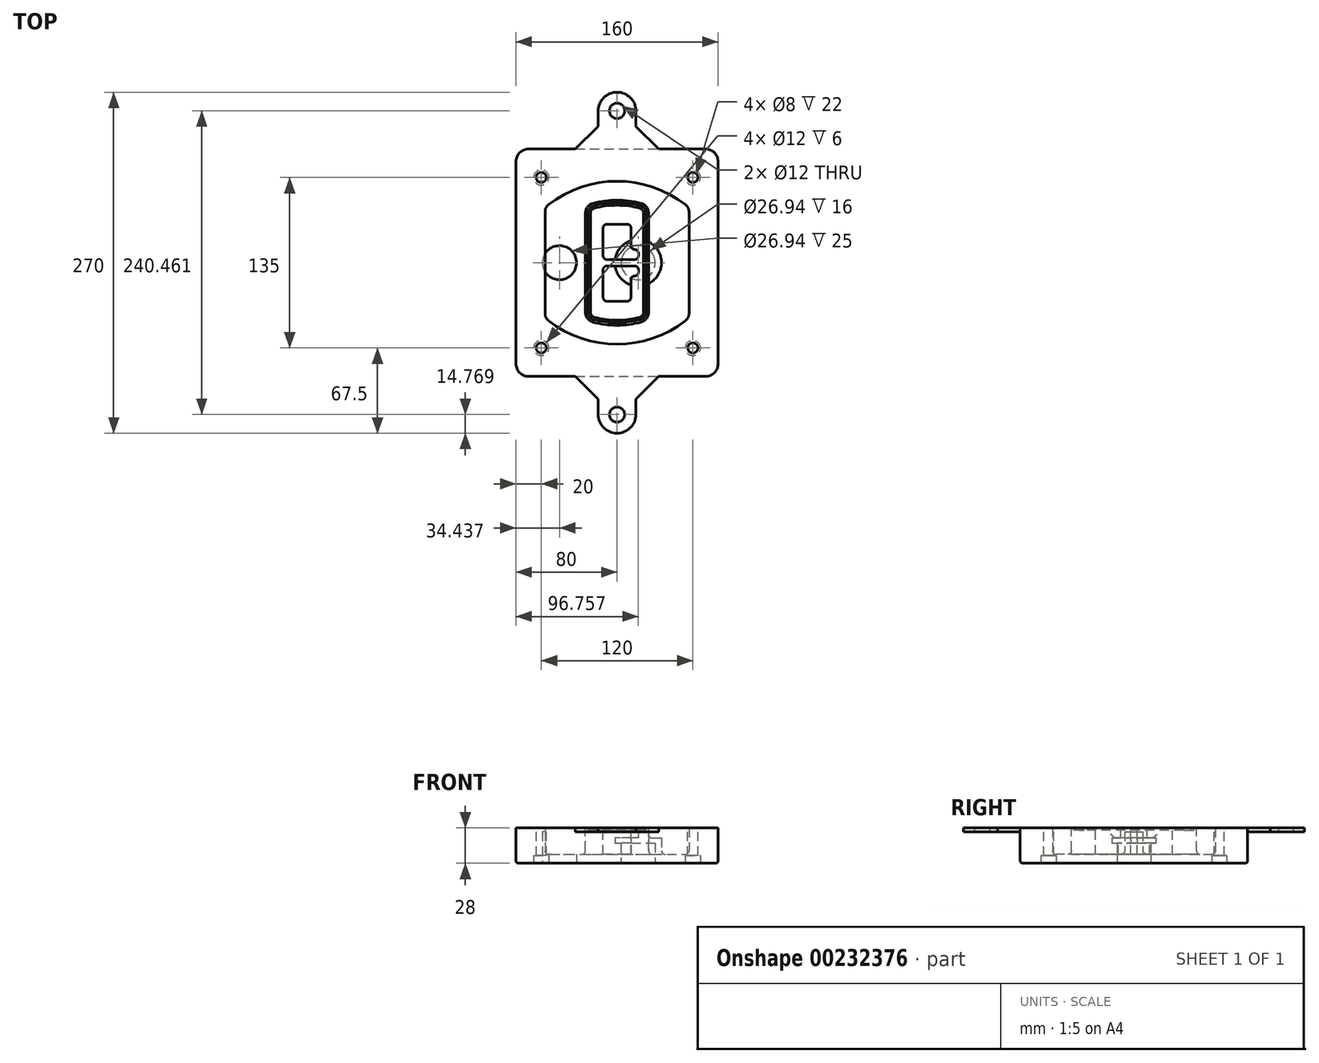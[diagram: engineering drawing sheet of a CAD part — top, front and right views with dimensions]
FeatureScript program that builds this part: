
annotation { "Feature Type Name" : "Feature", "Feature Type Description" : "" }
export const myFeature = defineFeature(function(context is Context, id is Id, definition is map)
    precondition{}
    {
        {
            var Q0;
            Q0=qCreatedBy(makeId("Top.planeOp"),FACE);
            var sketch = newSketch(context, id + "F0", { "sketchPlane" : qUnion([Q0])});
            skPoint(sketch, "E0.rect.middle", {"position": v(0, 0) * mm});
            skLineSegment(sketch, "E1.bottom", {"start": v(-70, -90) * mm, "end": v(70, -90) * mm});
            skLineSegment(sketch, "E1.top", {"start": v(-70, 90) * mm, "end": v(70, 90) * mm});
            skLineSegment(sketch, "E1.left", {"start": v(-80, -80) * mm, "end": v(-80, 80) * mm});
            skLineSegment(sketch, "E1.right", {"start": v(80, -80) * mm, "end": v(80, 80) * mm});
            skLineSegment(sketch, "E2", {"start": v(-80, 90) * mm, "end": v(80, -90) * mm, "construction": true});
            skLineSegment(sketch, "E3", {"start": v(80, 90) * mm, "end": v(-80, -90) * mm, "construction": true});
            skCircle(sketch, "E4", {"center": v(-60, 67.5) * mm, "radius": 4 * mm});
            skCircle(sketch, "E5", {"center": v(60, 67.5) * mm, "radius": 4 * mm});
            skCircle(sketch, "E6", {"center": v(60, -67.5) * mm, "radius": 4 * mm});
            skCircle(sketch, "E7", {"center": v(-60, -67.5) * mm, "radius": 4 * mm});
            skLineSegment(sketch, "E8", {"start": v(-60, 67.5) * mm, "end": v(60, 67.5) * mm, "construction": true});
            skLineSegment(sketch, "E9", {"start": v(60, 67.5) * mm, "end": v(60, -67.5) * mm, "construction": true});
            skLineSegment(sketch, "E10", {"start": v(60, -67.5) * mm, "end": v(-60, -67.5) * mm, "construction": true});
            skLineSegment(sketch, "E11", {"start": v(-60, -67.5) * mm, "end": v(-60, 67.5) * mm, "construction": true});
            skLineSegment(sketch, "E12", {"start": v(-60, 40.3) * mm, "end": v(-60, -40.3) * mm});
            skLineSegment(sketch, "E13", {"start": v(60, 40.3) * mm, "end": v(60, -40.3) * mm});
            skArc(sketch, "E14", {"start": v(56.15, 48.18) * mm, "mid": v(0, 67.5) * mm, "end": v(-56.15, 48.18) * mm});
            skArc(sketch, "E15", {"start": v(-56.15, -48.18) * mm, "mid": v(0, -67.5) * mm, "end": v(56.15, -48.18) * mm});
            skLineSegment(sketch, "E16", {"start": v(-60, 0) * mm, "end": v(60, 0) * mm, "construction": true});
            skPoint(sketch, "E17.visualSharp", {"position": v(-60, -45) * mm});
            skArc(sketch, "E17.filletArc", {"start": v(-60, -40.3) * mm, "mid": v(-58.99, -44.68) * mm, "end": v(-56.15, -48.18) * mm});
            skPoint(sketch, "E18.visualSharp", {"position": v(-60, 45) * mm});
            skArc(sketch, "E18.filletArc", {"start": v(-56.15, 48.18) * mm, "mid": v(-58.99, 44.68) * mm, "end": v(-60, 40.3) * mm});
            skPoint(sketch, "E19.visualSharp", {"position": v(60, 45) * mm});
            skArc(sketch, "E19.filletArc", {"start": v(60, 40.3) * mm, "mid": v(58.99, 44.68) * mm, "end": v(56.15, 48.18) * mm});
            skPoint(sketch, "E20.visualSharp", {"position": v(60, -45) * mm});
            skArc(sketch, "E20.filletArc", {"start": v(56.15, -48.18) * mm, "mid": v(58.99, -44.68) * mm, "end": v(60, -40.3) * mm});
            skPoint(sketch, "E21.visualSharp", {"position": v(-80, 90) * mm});
            skArc(sketch, "E21.filletArc", {"start": v(-70, 90) * mm, "mid": v(-77.07, 87.07) * mm, "end": v(-80, 80) * mm});
            skPoint(sketch, "E22.visualSharp", {"position": v(80, 90) * mm});
            skArc(sketch, "E22.filletArc", {"start": v(80, 80) * mm, "mid": v(77.07, 87.07) * mm, "end": v(70, 90) * mm});
            skPoint(sketch, "E23.visualSharp", {"position": v(80, -90) * mm});
            skArc(sketch, "E23.filletArc", {"start": v(70, -90) * mm, "mid": v(77.07, -87.07) * mm, "end": v(80, -80) * mm});
            skPoint(sketch, "E24.visualSharp", {"position": v(-80, -90) * mm});
            skArc(sketch, "E24.filletArc", {"start": v(-80, -80) * mm, "mid": v(-77.07, -87.07) * mm, "end": v(-70, -90) * mm});
            skArc(sketch, "E25.0", {"start": v(57, 40.3) * mm, "mid": v(56.3, 43.36) * mm, "end": v(54.3, 45.81) * mm});
            skLineSegment(sketch, "E25.1", {"start": v(57, 40.3) * mm, "end": v(57, -40.3) * mm});
            skArc(sketch, "E25.2", {"start": v(54.3, -45.81) * mm, "mid": v(56.3, -43.36) * mm, "end": v(57, -40.3) * mm});
            skArc(sketch, "E25.3", {"start": v(-54.3, -45.81) * mm, "mid": v(0, -64.5) * mm, "end": v(54.3, -45.81) * mm});
            skArc(sketch, "E25.4", {"start": v(-57, -40.3) * mm, "mid": v(-56.3, -43.36) * mm, "end": v(-54.3, -45.81) * mm});
            skArc(sketch, "E25.5", {"start": v(54.3, 45.81) * mm, "mid": v(0, 64.5) * mm, "end": v(-54.3, 45.81) * mm});
            skLineSegment(sketch, "E25.6", {"start": v(-57, 40.3) * mm, "end": v(-57, -40.3) * mm});
            skArc(sketch, "E25.7", {"start": v(-54.3, 45.81) * mm, "mid": v(-56.3, 43.36) * mm, "end": v(-57, 40.3) * mm});
            skArc(sketch, "E26.0", {"start": v(-58.62, 51.33) * mm, "mid": v(-62.58, 46.43) * mm, "end": v(-64, 40.3) * mm});
            skArc(sketch, "E26.1", {"start": v(58.62, 51.33) * mm, "mid": v(0, 71.5) * mm, "end": v(-58.62, 51.33) * mm});
            skArc(sketch, "E26.2", {"start": v(64, 40.3) * mm, "mid": v(62.58, 46.43) * mm, "end": v(58.62, 51.33) * mm});
            skLineSegment(sketch, "E26.3", {"start": v(64, 40.3) * mm, "end": v(64, -40.3) * mm});
            skArc(sketch, "E26.4", {"start": v(58.62, -51.33) * mm, "mid": v(62.58, -46.43) * mm, "end": v(64, -40.3) * mm});
            skLineSegment(sketch, "E26.5", {"start": v(-64, 40.3) * mm, "end": v(-64, -40.3) * mm});
            skArc(sketch, "E26.6", {"start": v(-58.62, -51.33) * mm, "mid": v(0, -71.5) * mm, "end": v(58.62, -51.33) * mm});
            skArc(sketch, "E26.7", {"start": v(-64, -40.3) * mm, "mid": v(-62.58, -46.43) * mm, "end": v(-58.62, -51.33) * mm});
            skSolve(sketch);
        }
        {
            var Q0;
            Q0=makeQuery(id+"F0.imprint","IMPRINT",FACE,{"disambiguationData":[TD([[makeQuery(id+"F0.imprint","IMPRINT",EDGE,{"derivedFrom":sQuery(id+"F0.wireOp",EDGE,"E1.bottom")}),1.0]])]});
            var Q1;
            Q1=makeQuery(id+"F0.imprint","IMPRINT",FACE,{"disambiguationData":[TD([[makeQuery(id+"F0.imprint","IMPRINT",EDGE,{"derivedFrom":sQuery(id+"F0.wireOp",EDGE,"E12")}),1.0]])]});
            var Q2;
            Q2=makeQuery(id+"F0.imprint","IMPRINT",FACE,{"disambiguationData":[TD([[makeQuery(id+"F0.imprint","IMPRINT",EDGE,{"derivedFrom":sQuery(id+"F0.wireOp",EDGE,"E25.0")}),1.0]])]});
            var Q3;
            Q3=makeQuery(id+"F0.imprint","IMPRINT",FACE,{"disambiguationData":[TD([[makeQuery(id+"F0.imprint","IMPRINT",EDGE,{"derivedFrom":sQuery(id+"F0.wireOp",EDGE,"E12")}),-1.0]])]});
            extrude(context, id + "F1", {"entities" : qUnion([Q0, Q1, Q2, Q3]), "oppositeDirection" : true, "depth" : 25 * mm});
        }
        {
            var Q0;
            Q0=makeQuery(id+"F0.imprint","IMPRINT",FACE,{"disambiguationData":[TD([[makeQuery(id+"F0.imprint","IMPRINT",EDGE,{"derivedFrom":sQuery(id+"F0.wireOp",EDGE,"E12")}),1.0]])]});
            extrude(context, id + "F2", {"entities" : qUnion([Q0]), "operationType" : NewBodyOperationType.ADD, "depth" : 3 * mm});
        }
        {
            var Q0;
            Q0=makeQuery(id+"F0.imprint","IMPRINT",FACE,{"disambiguationData":[TD([[makeQuery(id+"F0.imprint","IMPRINT",EDGE,{"derivedFrom":sQuery(id+"F0.wireOp",EDGE,"E25.0")}),1.0]])]});
            extrude(context, id + "F3", {"entities" : qUnion([Q0]), "operationType" : NewBodyOperationType.REMOVE, "oppositeDirection" : true, "depth" : 18 * mm});
        }
        {
            var Q0;
            Q0=makeQuery(id+"F2.opExtrude","CAP_FACE",FACE,{"disambiguationData":[OSD([sQuery(id+"F0.wireOp",EDGE,"E12"),sQuery(id+"F0.wireOp",EDGE,"E13"),sQuery(id+"F0.wireOp",EDGE,"E14"),sQuery(id+"F0.wireOp",EDGE,"E15"),sQuery(id+"F0.wireOp",EDGE,"E17.filletArc"),sQuery(id+"F0.wireOp",EDGE,"E18.filletArc"),sQuery(id+"F0.wireOp",EDGE,"E19.filletArc"),sQuery(id+"F0.wireOp",EDGE,"E20.filletArc"),sQuery(id+"F0.wireOp",EDGE,"E25.0"),sQuery(id+"F0.wireOp",EDGE,"E25.1"),sQuery(id+"F0.wireOp",EDGE,"E25.2"),sQuery(id+"F0.wireOp",EDGE,"E25.3"),sQuery(id+"F0.wireOp",EDGE,"E25.4"),sQuery(id+"F0.wireOp",EDGE,"E25.5"),sQuery(id+"F0.wireOp",EDGE,"E25.6"),sQuery(id+"F0.wireOp",EDGE,"E25.7")])],"isStart":false});
            var sketch = newSketch(context, id + "F4", { "sketchPlane" : qUnion([Q0])});
            skArc(sketch, "E27.0", {"start": v(-19.08, -46.97) * mm, "mid": v(0, -49.5) * mm, "end": v(19.08, -46.97) * mm});
            skArc(sketch, "E28.0", {"start": v(19.08, 46.97) * mm, "mid": v(0, 49.5) * mm, "end": v(-19.08, 46.97) * mm});
            skLineSegment(sketch, "E29", {"start": v(-25, 39.25) * mm, "end": v(-25, -39.25) * mm});
            skLineSegment(sketch, "E30", {"start": v(25, 39.25) * mm, "end": v(25, -39.25) * mm});
            skLineSegment(sketch, "E31", {"start": v(-25, 45.1) * mm, "end": v(25, 45.1) * mm, "construction": true});
            skLineSegment(sketch, "E32", {"start": v(-25, -45.1) * mm, "end": v(25, -45.1) * mm, "construction": true});
            skPoint(sketch, "E33.visualSharp", {"position": v(-25, 45.1) * mm});
            skArc(sketch, "E33.filletArc", {"start": v(-19.08, 46.97) * mm, "mid": v(-23.35, 44.11) * mm, "end": v(-25, 39.25) * mm});
            skPoint(sketch, "E34.visualSharp", {"position": v(25, 45.1) * mm});
            skArc(sketch, "E34.filletArc", {"start": v(25, 39.25) * mm, "mid": v(23.35, 44.11) * mm, "end": v(19.08, 46.97) * mm});
            skPoint(sketch, "E35.visualSharp", {"position": v(25, -45.1) * mm});
            skArc(sketch, "E35.filletArc", {"start": v(19.08, -46.97) * mm, "mid": v(23.35, -44.11) * mm, "end": v(25, -39.25) * mm});
            skPoint(sketch, "E36.visualSharp", {"position": v(-25, -45.1) * mm});
            skArc(sketch, "E36.filletArc", {"start": v(-25, -39.25) * mm, "mid": v(-23.35, -44.11) * mm, "end": v(-19.08, -46.97) * mm});
            skArc(sketch, "E37.0", {"start": v(54.3, 45.81) * mm, "mid": v(0, 64.5) * mm, "end": v(-54.3, 45.81) * mm});
            skArc(sketch, "E37.1", {"start": v(-54.3, 45.81) * mm, "mid": v(-56.3, 43.36) * mm, "end": v(-57, 40.3) * mm});
            skLineSegment(sketch, "E37.2", {"start": v(-57, 40.3) * mm, "end": v(-57, -40.3) * mm});
            skArc(sketch, "E37.3", {"start": v(-57, -40.3) * mm, "mid": v(-56.3, -43.36) * mm, "end": v(-54.3, -45.81) * mm});
            skArc(sketch, "E37.4", {"start": v(-54.3, -45.81) * mm, "mid": v(0, -64.5) * mm, "end": v(54.3, -45.81) * mm});
            skArc(sketch, "E37.5", {"start": v(54.3, -45.81) * mm, "mid": v(56.3, -43.36) * mm, "end": v(57, -40.3) * mm});
            skLineSegment(sketch, "E37.6", {"start": v(57, 40.3) * mm, "end": v(57, -40.3) * mm});
            skArc(sketch, "E37.7", {"start": v(57, 40.3) * mm, "mid": v(56.3, 43.36) * mm, "end": v(54.3, 45.81) * mm});
            skLineSegment(sketch, "E38.0", {"start": v(23, 39.25) * mm, "end": v(23, -39.25) * mm});
            skArc(sketch, "E38.1", {"start": v(18.56, -45.04) * mm, "mid": v(21.76, -42.9) * mm, "end": v(23, -39.25) * mm});
            skArc(sketch, "E38.2", {"start": v(-18.56, -45.04) * mm, "mid": v(0, -47.5) * mm, "end": v(18.56, -45.04) * mm});
            skArc(sketch, "E38.3", {"start": v(-23, -39.25) * mm, "mid": v(-21.76, -42.9) * mm, "end": v(-18.56, -45.04) * mm});
            skLineSegment(sketch, "E38.4", {"start": v(-23, 39.25) * mm, "end": v(-23, -39.25) * mm});
            skArc(sketch, "E38.5", {"start": v(23, 39.25) * mm, "mid": v(21.76, 42.9) * mm, "end": v(18.56, 45.04) * mm});
            skArc(sketch, "E38.6", {"start": v(-18.56, 45.04) * mm, "mid": v(-21.76, 42.9) * mm, "end": v(-23, 39.25) * mm});
            skArc(sketch, "E38.7", {"start": v(18.56, 45.04) * mm, "mid": v(0, 47.5) * mm, "end": v(-18.56, 45.04) * mm});
            skArc(sketch, "E39.0", {"start": v(21, 39.25) * mm, "mid": v(20.18, 41.68) * mm, "end": v(18.04, 43.1) * mm});
            skLineSegment(sketch, "E39.1", {"start": v(21, 39.25) * mm, "end": v(21, -39.25) * mm});
            skArc(sketch, "E39.2", {"start": v(18.04, -43.1) * mm, "mid": v(20.18, -41.68) * mm, "end": v(21, -39.25) * mm});
            skArc(sketch, "E39.3", {"start": v(-18.04, -43.1) * mm, "mid": v(0, -45.5) * mm, "end": v(18.04, -43.1) * mm});
            skArc(sketch, "E39.4", {"start": v(-21, -39.25) * mm, "mid": v(-20.18, -41.68) * mm, "end": v(-18.04, -43.1) * mm});
            skArc(sketch, "E39.5", {"start": v(18.04, 43.1) * mm, "mid": v(0, 45.5) * mm, "end": v(-18.04, 43.1) * mm});
            skLineSegment(sketch, "E39.6", {"start": v(-21, 39.25) * mm, "end": v(-21, -39.25) * mm});
            skArc(sketch, "E39.7", {"start": v(-18.04, 43.1) * mm, "mid": v(-20.18, 41.68) * mm, "end": v(-21, 39.25) * mm});
            skLineSegment(sketch, "E40", {"start": v(-25, 0) * mm, "end": v(25, 0) * mm, "construction": true});
            skLineSegment(sketch, "E41", {"start": v(-11, 5.5) * mm, "end": v(-11, 27.5) * mm});
            skLineSegment(sketch, "E42", {"start": v(-8, 30.5) * mm, "end": v(8, 30.5) * mm});
            skLineSegment(sketch, "E43", {"start": v(11, 27.5) * mm, "end": v(11, 13.5) * mm});
            skLineSegment(sketch, "E44", {"start": v(14, 10.5) * mm, "end": v(14, 10.5) * mm});
            skLineSegment(sketch, "E45", {"start": v(17, 7.5) * mm, "end": v(17, 5.5) * mm});
            skLineSegment(sketch, "E46", {"start": v(14, 2.5) * mm, "end": v(-8, 2.5) * mm});
            skPoint(sketch, "E47.visualSharp", {"position": v(-11, 30.5) * mm});
            skArc(sketch, "E47.filletArc", {"start": v(-8, 30.5) * mm, "mid": v(-10.12, 29.62) * mm, "end": v(-11, 27.5) * mm});
            skPoint(sketch, "E48.visualSharp", {"position": v(11, 30.5) * mm});
            skArc(sketch, "E48.filletArc", {"start": v(11, 27.5) * mm, "mid": v(10.12, 29.62) * mm, "end": v(8, 30.5) * mm});
            skPoint(sketch, "E49.visualSharp", {"position": v(11, 10.5) * mm});
            skArc(sketch, "E49.filletArc", {"start": v(11, 13.5) * mm, "mid": v(11.88, 11.38) * mm, "end": v(14, 10.5) * mm});
            skPoint(sketch, "E50.visualSharp", {"position": v(17, 10.5) * mm});
            skArc(sketch, "E50.filletArc", {"start": v(17, 7.5) * mm, "mid": v(16.12, 9.62) * mm, "end": v(14, 10.5) * mm});
            skPoint(sketch, "E51.visualSharp", {"position": v(17, 2.5) * mm});
            skArc(sketch, "E51.filletArc", {"start": v(14, 2.5) * mm, "mid": v(16.12, 3.38) * mm, "end": v(17, 5.5) * mm});
            skPoint(sketch, "E52.visualSharp", {"position": v(-11, 2.5) * mm});
            skArc(sketch, "E52.filletArc", {"start": v(-11, 5.5) * mm, "mid": v(-10.12, 3.38) * mm, "end": v(-8, 2.5) * mm});
            skLineSegment(sketch, "E53.0.MirrorCS", {"start": v(14, -2.5) * mm, "end": v(-8, -2.5) * mm});
            skArc(sketch, "E54.0.MirrorCS", {"start": v(-11, -5.5) * mm, "mid": v(-10.12, -3.38) * mm, "end": v(-8, -2.5) * mm});
            skLineSegment(sketch, "E55.0.MirrorCS", {"start": v(-11, -5.5) * mm, "end": v(-11, -27.5) * mm});
            skArc(sketch, "E56.0.MirrorCS", {"start": v(-8, -30.5) * mm, "mid": v(-10.12, -29.62) * mm, "end": v(-11, -27.5) * mm});
            skLineSegment(sketch, "E57.0.MirrorCS", {"start": v(-8, -30.5) * mm, "end": v(8, -30.5) * mm});
            skArc(sketch, "E58.0.MirrorCS", {"start": v(11, -27.5) * mm, "mid": v(10.12, -29.62) * mm, "end": v(8, -30.5) * mm});
            skLineSegment(sketch, "E59.0.MirrorCS", {"start": v(11, -27.5) * mm, "end": v(11, -13.5) * mm});
            skArc(sketch, "E60.0.MirrorCS", {"start": v(11, -13.5) * mm, "mid": v(11.88, -11.38) * mm, "end": v(14, -10.5) * mm});
            skArc(sketch, "E61.0.MirrorCS", {"start": v(17, -7.5) * mm, "mid": v(16.12, -9.62) * mm, "end": v(14, -10.5) * mm});
            skLineSegment(sketch, "E62.0.MirrorCS", {"start": v(17, -7.5) * mm, "end": v(17, -5.5) * mm});
            skArc(sketch, "E63.0.MirrorCS", {"start": v(14, -2.5) * mm, "mid": v(16.12, -3.38) * mm, "end": v(17, -5.5) * mm});
            skSolve(sketch);
        }
        {
            var Q0;
            Q0=makeQuery(id+"F4.imprint","IMPRINT",FACE,{"disambiguationData":[TD([[makeQuery(id+"F4.imprint","IMPRINT",EDGE,{"derivedFrom":sQuery(id+"F4.wireOp",EDGE,"E27.0")}),1.0]])]});
            var Q1;
            Q1=makeQuery(id+"F4.imprint","IMPRINT",FACE,{"disambiguationData":[TD([[makeQuery(id+"F4.imprint","IMPRINT",EDGE,{"derivedFrom":sQuery(id+"F4.wireOp",EDGE,"E38.0")}),-1.0]])]});
            var Q2;
            Q2=makeQuery(id+"F4.imprint","IMPRINT",FACE,{"disambiguationData":[TD([[makeQuery(id+"F4.imprint","IMPRINT",EDGE,{"derivedFrom":sQuery(id+"F4.wireOp",EDGE,"E39.0")}),1.0]])]});
            extrude(context, id + "F5", {"entities" : qUnion([Q0, Q1, Q2]), "operationType" : NewBodyOperationType.ADD, "endBound" : BoundingType.UP_TO_NEXT, "oppositeDirection" : true, "depth" : 25 * mm});
        }
        {
            var Q0;
            Q0=makeQuery(id+"F4.imprint","IMPRINT",FACE,{"disambiguationData":[TD([[makeQuery(id+"F4.imprint","IMPRINT",EDGE,{"derivedFrom":sQuery(id+"F4.wireOp",EDGE,"E38.0")}),-1.0]])]});
            extrude(context, id + "F6", {"entities" : qUnion([Q0]), "operationType" : NewBodyOperationType.REMOVE, "oppositeDirection" : true, "depth" : 2 * mm});
        }
        {
            var Q0;
            Q0=makeQuery(id+"F1.opExtrude","CAP_FACE",FACE,{"disambiguationData":[OSD([sQuery(id+"F0.wireOp",EDGE,"E1.bottom"),sQuery(id+"F0.wireOp",EDGE,"E1.top"),sQuery(id+"F0.wireOp",EDGE,"E1.left"),sQuery(id+"F0.wireOp",EDGE,"E1.right"),sQuery(id+"F0.wireOp",EDGE,"E4"),sQuery(id+"F0.wireOp",EDGE,"E5"),sQuery(id+"F0.wireOp",EDGE,"E6"),sQuery(id+"F0.wireOp",EDGE,"E7"),sQuery(id+"F0.wireOp",EDGE,"E21.filletArc"),sQuery(id+"F0.wireOp",EDGE,"E22.filletArc"),sQuery(id+"F0.wireOp",EDGE,"E23.filletArc"),sQuery(id+"F0.wireOp",EDGE,"E24.filletArc")])],"isStart":false});
            var sketch = newSketch(context, id + "F7", { "sketchPlane" : qUnion([Q0])});
            skCircle(sketch, "E64", {"center": v(16.76, 0) * mm, "radius": 13.47 * mm});
            skCircle(sketch, "E65", {"center": v(-45.56, 0) * mm, "radius": 13.47 * mm});
            skLineSegment(sketch, "E66", {"start": v(80, 0) * mm, "end": v(-80, 0) * mm});
            skCircle(sketch, "E67", {"center": v(16.76, 0) * mm, "radius": 18.47 * mm});
            skCircle(sketch, "E68", {"center": v(60, -67.5) * mm, "radius": 6 * mm});
            skCircle(sketch, "E69", {"center": v(-60, -67.5) * mm, "radius": 6 * mm});
            skCircle(sketch, "E70", {"center": v(-60, 67.5) * mm, "radius": 6 * mm});
            skCircle(sketch, "E71", {"center": v(60, 67.5) * mm, "radius": 6 * mm});
            skSolve(sketch);
        }
        {
            var Q0;
            {var subQ1=sQuery(id+"F7.wireOp",EDGE,"E66");var subQ4=sQuery(id+"F7.wireOp",EDGE,"E64");var subQ6=makeQuery(id+"F7.imprint","INTERSECT",VERTEX,{"disambiguationData":[OD(0.0)],"derivedFrom":[subQ4,subQ1]});Q0=makeQuery(id+"F7.imprint","IMPRINT",FACE,{"disambiguationData":[TD([[makeQuery(id+"F7.imprint","IMPRINT",EDGE,{"disambiguationData":[TD([[subQ6,-1.0]])],"derivedFrom":subQ4}),-1.0]])]});}
            var Q1;
            {var subQ0=sQuery(id+"F7.wireOp",EDGE,"E66");var subQ1=sQuery(id+"F7.wireOp",EDGE,"E64");var subQ3=makeQuery(id+"F7.imprint","INTERSECT",VERTEX,{"disambiguationData":[OD(0.0)],"derivedFrom":[subQ1,subQ0]});Q1=makeQuery(id+"F7.imprint","IMPRINT",FACE,{"disambiguationData":[TD([[makeQuery(id+"F7.imprint","IMPRINT",EDGE,{"disambiguationData":[TD([[subQ3,-1.0]])],"derivedFrom":subQ1}),1.0]])]});}
            var Q2;
            {var subQ0=sQuery(id+"F7.wireOp",EDGE,"E66");var subQ1=sQuery(id+"F7.wireOp",EDGE,"E64");var subQ3=makeQuery(id+"F7.imprint","INTERSECT",VERTEX,{"disambiguationData":[OD(0.0)],"derivedFrom":[subQ1,subQ0]});Q2=makeQuery(id+"F7.imprint","IMPRINT",FACE,{"disambiguationData":[TD([[makeQuery(id+"F7.imprint","IMPRINT",EDGE,{"disambiguationData":[TD([[subQ3,1.0]])],"derivedFrom":subQ1}),1.0]])]});}
            var Q3;
            {var subQ1=sQuery(id+"F7.wireOp",EDGE,"E66");var subQ4=sQuery(id+"F7.wireOp",EDGE,"E64");var subQ6=makeQuery(id+"F7.imprint","INTERSECT",VERTEX,{"disambiguationData":[OD(0.0)],"derivedFrom":[subQ4,subQ1]});Q3=makeQuery(id+"F7.imprint","IMPRINT",FACE,{"disambiguationData":[TD([[makeQuery(id+"F7.imprint","IMPRINT",EDGE,{"disambiguationData":[TD([[subQ6,1.0]])],"derivedFrom":subQ4}),-1.0]])]});}
            extrude(context, id + "F8", {"entities" : qUnion([Q0, Q1, Q2, Q3]), "operationType" : NewBodyOperationType.ADD, "oppositeDirection" : true, "depth" : 20 * mm});
        }
        {
            var Q0;
            {var subQ0=sQuery(id+"F7.wireOp",EDGE,"E66");var subQ1=sQuery(id+"F7.wireOp",EDGE,"E64");var subQ3=makeQuery(id+"F7.imprint","INTERSECT",VERTEX,{"disambiguationData":[OD(0.0)],"derivedFrom":[subQ1,subQ0]});Q0=makeQuery(id+"F7.imprint","IMPRINT",FACE,{"disambiguationData":[TD([[makeQuery(id+"F7.imprint","IMPRINT",EDGE,{"disambiguationData":[TD([[subQ3,-1.0]])],"derivedFrom":subQ1}),1.0]])]});}
            var Q1;
            {var subQ0=sQuery(id+"F7.wireOp",EDGE,"E66");var subQ1=sQuery(id+"F7.wireOp",EDGE,"E64");var subQ3=makeQuery(id+"F7.imprint","INTERSECT",VERTEX,{"disambiguationData":[OD(0.0)],"derivedFrom":[subQ1,subQ0]});Q1=makeQuery(id+"F7.imprint","IMPRINT",FACE,{"disambiguationData":[TD([[makeQuery(id+"F7.imprint","IMPRINT",EDGE,{"disambiguationData":[TD([[subQ3,1.0]])],"derivedFrom":subQ1}),1.0]])]});}
            extrude(context, id + "F9", {"entities" : qUnion([Q0, Q1]), "operationType" : NewBodyOperationType.REMOVE, "oppositeDirection" : true, "depth" : 16 * mm});
        }
        {
            var Q0;
            {var subQ0=sQuery(id+"F7.wireOp",EDGE,"E66");var subQ1=sQuery(id+"F7.wireOp",EDGE,"E65");var subQ3=makeQuery(id+"F7.imprint","INTERSECT",VERTEX,{"disambiguationData":[OD(0.0)],"derivedFrom":[subQ1,subQ0]});Q0=makeQuery(id+"F7.imprint","IMPRINT",FACE,{"disambiguationData":[TD([[makeQuery(id+"F7.imprint","IMPRINT",EDGE,{"disambiguationData":[TD([[subQ3,-1.0]])],"derivedFrom":subQ1}),1.0]])]});}
            var Q1;
            {var subQ0=sQuery(id+"F7.wireOp",EDGE,"E66");var subQ1=sQuery(id+"F7.wireOp",EDGE,"E65");var subQ3=makeQuery(id+"F7.imprint","INTERSECT",VERTEX,{"disambiguationData":[OD(0.0)],"derivedFrom":[subQ1,subQ0]});Q1=makeQuery(id+"F7.imprint","IMPRINT",FACE,{"disambiguationData":[TD([[makeQuery(id+"F7.imprint","IMPRINT",EDGE,{"disambiguationData":[TD([[subQ3,1.0]])],"derivedFrom":subQ1}),1.0]])]});}
            extrude(context, id + "F10", {"entities" : qUnion([Q0, Q1]), "operationType" : NewBodyOperationType.REMOVE, "oppositeDirection" : true, "depth" : 25 * mm});
        }
        {
            var Q0;
            Q0=makeQuery(id+"F7.imprint","IMPRINT",FACE,{"disambiguationData":[TD([[makeQuery(id+"F7.imprint","IMPRINT",EDGE,{"derivedFrom":sQuery(id+"F7.wireOp",EDGE,"E68")}),1.0]])]});
            var Q1;
            Q1=makeQuery(id+"F7.imprint","IMPRINT",FACE,{"disambiguationData":[TD([[makeQuery(id+"F7.imprint","IMPRINT",EDGE,{"derivedFrom":makeQuery(id+"F1.opExtrude","CAP_EDGE",EDGE,{"disambiguationData":[OSD([sQuery(id+"F0.wireOp",EDGE,"E5")])],"isStart":false})}),-1.0]])]});
            var Q2;
            Q2=makeQuery(id+"F7.imprint","IMPRINT",FACE,{"disambiguationData":[TD([[makeQuery(id+"F7.imprint","IMPRINT",EDGE,{"derivedFrom":sQuery(id+"F7.wireOp",EDGE,"E69")}),1.0]])]});
            var Q3;
            Q3=makeQuery(id+"F7.imprint","IMPRINT",FACE,{"disambiguationData":[TD([[makeQuery(id+"F7.imprint","IMPRINT",EDGE,{"derivedFrom":makeQuery(id+"F1.opExtrude","CAP_EDGE",EDGE,{"disambiguationData":[OSD([sQuery(id+"F0.wireOp",EDGE,"E4")])],"isStart":false})}),-1.0]])]});
            var Q4;
            Q4=makeQuery(id+"F7.imprint","IMPRINT",FACE,{"disambiguationData":[TD([[makeQuery(id+"F7.imprint","IMPRINT",EDGE,{"derivedFrom":sQuery(id+"F7.wireOp",EDGE,"E70")}),1.0]])]});
            var Q5;
            Q5=makeQuery(id+"F7.imprint","IMPRINT",FACE,{"disambiguationData":[TD([[makeQuery(id+"F7.imprint","IMPRINT",EDGE,{"derivedFrom":makeQuery(id+"F1.opExtrude","CAP_EDGE",EDGE,{"disambiguationData":[OSD([sQuery(id+"F0.wireOp",EDGE,"E7")])],"isStart":false})}),-1.0]])]});
            var Q6;
            Q6=makeQuery(id+"F7.imprint","IMPRINT",FACE,{"disambiguationData":[TD([[makeQuery(id+"F7.imprint","IMPRINT",EDGE,{"derivedFrom":sQuery(id+"F7.wireOp",EDGE,"E71")}),1.0]])]});
            var Q7;
            Q7=makeQuery(id+"F7.imprint","IMPRINT",FACE,{"disambiguationData":[TD([[makeQuery(id+"F7.imprint","IMPRINT",EDGE,{"derivedFrom":makeQuery(id+"F1.opExtrude","CAP_EDGE",EDGE,{"disambiguationData":[OSD([sQuery(id+"F0.wireOp",EDGE,"E6")])],"isStart":false})}),-1.0]])]});
            extrude(context, id + "F11", {"entities" : qUnion([Q0, Q1, Q2, Q3, Q4, Q5, Q6, Q7]), "operationType" : NewBodyOperationType.REMOVE, "oppositeDirection" : true, "depth" : 6 * mm});
        }
        {
            var Q0;
            Q0=makeQuery(id+"F9.boolean.opBoolean","COPY",FACE,{"derivedFrom":makeQuery(id+"F9.opExtrude","CAP_FACE",FACE,{"disambiguationData":[OSD([sQuery(id+"F7.wireOp",EDGE,"E64")])],"isStart":false})});
            var sketch = newSketch(context, id + "F12", { "sketchPlane" : qUnion([Q0])});
            skArc(sketch, "E72.0", {"start": v(11, 17.55) * mm, "mid": v(2.57, 11.82) * mm, "end": v(-1.54, 2.5) * mm});
            skArc(sketch, "E72.1", {"start": v(-1.54, -2.5) * mm, "mid": v(2.57, -11.82) * mm, "end": v(11, -17.55) * mm});
            skLineSegment(sketch, "E73", {"start": v(-1.54, -2.5) * mm, "end": v(14, -2.5) * mm});
            skLineSegment(sketch, "E74.0", {"start": v(14, 2.5) * mm, "end": v(-1.54, 2.5) * mm});
            skArc(sketch, "E74.1", {"start": v(14, 2.5) * mm, "mid": v(16.12, 3.38) * mm, "end": v(17, 5.5) * mm});
            skLineSegment(sketch, "E74.2", {"start": v(17, 7.5) * mm, "end": v(17, 5.5) * mm});
            skArc(sketch, "E74.3", {"start": v(17, 7.5) * mm, "mid": v(16.12, 9.62) * mm, "end": v(14, 10.5) * mm});
            skArc(sketch, "E74.4", {"start": v(11, 13.5) * mm, "mid": v(11.88, 11.38) * mm, "end": v(14, 10.5) * mm});
            skLineSegment(sketch, "E74.5", {"start": v(11, 17.55) * mm, "end": v(11, 13.5) * mm});
            skLineSegment(sketch, "E74.7", {"start": v(14, -2.5) * mm, "end": v(-1.54, -2.5) * mm});
            skArc(sketch, "E74.8", {"start": v(14, -2.5) * mm, "mid": v(16.12, -3.38) * mm, "end": v(17, -5.5) * mm});
            skLineSegment(sketch, "E74.9", {"start": v(17, -7.5) * mm, "end": v(17, -5.5) * mm});
            skArc(sketch, "E74.10", {"start": v(17, -7.5) * mm, "mid": v(16.12, -9.62) * mm, "end": v(14, -10.5) * mm});
            skArc(sketch, "E74.11", {"start": v(11, -13.5) * mm, "mid": v(11.88, -11.38) * mm, "end": v(14, -10.5) * mm});
            skLineSegment(sketch, "E74.12", {"start": v(11, -17.55) * mm, "end": v(11, -13.5) * mm});
            skPoint(sketch, "E75.orphan", {"position": v(11, -27.5) * mm});
            skPoint(sketch, "E76.orphan", {"position": v(-8, -2.5) * mm});
            skPoint(sketch, "E77.orphan", {"position": v(-8, 2.5) * mm});
            skPoint(sketch, "E78.orphan", {"position": v(11, 27.5) * mm});
            skSolve(sketch);
        }
        {
            var Q0;
            {var subQ7=sQuery(id+"F12.wireOp",EDGE,"E72.0");var subQ14=sQuery(id+"F12.wireOp",EDGE,"E72.1");var subQ16=sQuery(id+"F12.wireOp",EDGE,"E74.1");var subQ18=sQuery(id+"F12.wireOp",EDGE,"E74.8");Q0=qUnion([makeQuery(id+"F12.imprint","IMPRINT",FACE,{"disambiguationData":[TD([[makeQuery(id+"F12.imprint","IMPRINT",EDGE,{"derivedFrom":subQ7}),1.0]])]}),makeQuery(id+"F12.imprint","IMPRINT",FACE,{"disambiguationData":[TD([[makeQuery(id+"F12.imprint","IMPRINT",EDGE,{"derivedFrom":subQ14}),1.0]])]}),makeQuery(id+"F12.imprint","IMPRINT",FACE,{"disambiguationData":[TD([[makeQuery(id+"F12.imprint","IMPRINT",EDGE,{"derivedFrom":subQ16}),1.0]])]}),makeQuery(id+"F12.imprint","IMPRINT",FACE,{"disambiguationData":[TD([[makeQuery(id+"F12.imprint","IMPRINT",EDGE,{"derivedFrom":subQ18}),-1.0]])]})]);}
            var Q1;
            Q1=makeQuery(id+"F5.boolean.opBoolean","SPLIT",FACE,{"disambiguationData":[TD([makeQuery(id+"F5.opExtrude","SWEPT_FACE",FACE,{"disambiguationData":[OSD([sQuery(id+"F4.wireOp",EDGE,"E41")])]})])],"derivedFrom":makeQuery(id+"F3.boolean.opBoolean","COPY",FACE,{"derivedFrom":makeQuery(id+"F3.opExtrude","CAP_FACE",FACE,{"disambiguationData":[OSD([sQuery(id+"F0.wireOp",EDGE,"E25.0"),sQuery(id+"F0.wireOp",EDGE,"E25.1"),sQuery(id+"F0.wireOp",EDGE,"E25.2"),sQuery(id+"F0.wireOp",EDGE,"E25.3"),sQuery(id+"F0.wireOp",EDGE,"E25.4"),sQuery(id+"F0.wireOp",EDGE,"E25.5"),sQuery(id+"F0.wireOp",EDGE,"E25.6"),sQuery(id+"F0.wireOp",EDGE,"E25.7")])],"isStart":false})})});
            extrude(context, id + "F13", {"entities" : qUnion([Q0]), "operationType" : NewBodyOperationType.REMOVE, "endBound" : BoundingType.UP_TO_SURFACE, "endBoundEntityFace" : qUnion([Q1]), "depth" : 25 * mm});
        }
        {
            var Q0;
            Q0=makeQuery(id+"F3.boolean.opBoolean","COPY",EDGE,{"derivedFrom":makeQuery(id+"F3.opExtrude","CAP_EDGE",EDGE,{"disambiguationData":[OSD([sQuery(id+"F0.wireOp",EDGE,"E25.6")])],"isStart":false})});
            var Q1;
            Q1=makeQuery(id+"F8.boolean.opBoolean","INTERSECT",EDGE,{"derivedFrom":[makeQuery(id+"F5.opExtrude","SWEPT_FACE",FACE,{"disambiguationData":[OSD([sQuery(id+"F4.wireOp",EDGE,"E30")])]}),makeQuery(id+"F8.opExtrude","CAP_FACE",FACE,{"disambiguationData":[OSD([sQuery(id+"F7.wireOp",EDGE,"E67")])],"isStart":false})]});
            var Q2;
            Q2=makeQuery(id+"F8.boolean.opBoolean","INTERSECT",EDGE,{"disambiguationData":[OD(1.0)],"derivedFrom":[makeQuery(id+"F5.opExtrude","SWEPT_FACE",FACE,{"disambiguationData":[OSD([sQuery(id+"F4.wireOp",EDGE,"E30")])]}),makeQuery(id+"F8.opExtrude","SWEPT_FACE",FACE,{"disambiguationData":[OSD([sQuery(id+"F7.wireOp",EDGE,"E67")])]})]});
            var Q3;
            {var subQ0=sQuery(id+"F4.wireOp",EDGE,"E30");Q3=makeQuery(id+"F8.boolean.opBoolean","SPLIT",EDGE,{"disambiguationData":[TD([makeQuery(id+"F5.opExtrude","SWEPT_FACE",FACE,{"disambiguationData":[OSD([sQuery(id+"F4.wireOp",EDGE,"E35.filletArc")])]})])],"derivedFrom":makeQuery(id+"F5.opExtrude","CAP_EDGE",EDGE,{"disambiguationData":[OSD([subQ0])],"isStart":false})});}
            var Q4;
            {var subQ0=sQuery(id+"F0.wireOp",EDGE,"E25.7");var subQ1=sQuery(id+"F0.wireOp",EDGE,"E25.1");var subQ2=sQuery(id+"F0.wireOp",EDGE,"E25.6");var subQ3=sQuery(id+"F0.wireOp",EDGE,"E25.5");var subQ4=sQuery(id+"F0.wireOp",EDGE,"E25.4");var subQ5=sQuery(id+"F0.wireOp",EDGE,"E25.0");var subQ6=sQuery(id+"F0.wireOp",EDGE,"E25.2");var subQ7=sQuery(id+"F0.wireOp",EDGE,"E25.3");Q4=makeQuery(id+"F8.boolean.opBoolean","INTERSECT",EDGE,{"derivedFrom":[makeQuery(id+"F5.boolean.opBoolean","SPLIT",FACE,{"disambiguationData":[TD([makeQuery(id+"F2.opExtrude","SWEPT_FACE",FACE,{"disambiguationData":[OSD([subQ5])]})])],"derivedFrom":makeQuery(id+"F3.boolean.opBoolean","COPY",FACE,{"derivedFrom":makeQuery(id+"F3.opExtrude","CAP_FACE",FACE,{"disambiguationData":[OSD([subQ5,subQ1,subQ6,subQ7,subQ4,subQ3,subQ2,subQ0])],"isStart":false})})}),makeQuery(id+"F8.opExtrude","SWEPT_FACE",FACE,{"disambiguationData":[OSD([sQuery(id+"F7.wireOp",EDGE,"E67")])]})]});}
            var Q5;
            Q5=makeQuery(id+"F8.boolean.opBoolean","INTERSECT",EDGE,{"disambiguationData":[OD(0.0)],"derivedFrom":[makeQuery(id+"F5.opExtrude","SWEPT_FACE",FACE,{"disambiguationData":[OSD([sQuery(id+"F4.wireOp",EDGE,"E30")])]}),makeQuery(id+"F8.opExtrude","SWEPT_FACE",FACE,{"disambiguationData":[OSD([sQuery(id+"F7.wireOp",EDGE,"E67")])]})]});
            fillet(context, id + "F14", {"entities" : qUnion([Q0, Q1, Q2, Q3, Q4, Q5]), "radius" : 3 * mm, "tangentPropagation" : true, "allowEdgeOverflow" : false});
        }
        {
            var Q0;
            Q0=makeQuery(id+"F1.opExtrude","CAP_EDGE",EDGE,{"disambiguationData":[OSD([sQuery(id+"F0.wireOp",EDGE,"E1.bottom")])],"isStart":false});
            fillet(context, id + "F15", {"entities" : qUnion([Q0]), "radius" : 2 * mm, "tangentPropagation" : true, "allowEdgeOverflow" : false});
        }
        {
            var Q0;
            {var subQ0=sQuery(id+"F0.wireOp",EDGE,"E22.filletArc");var subQ1=sQuery(id+"F0.wireOp",EDGE,"E7");var subQ2=sQuery(id+"F0.wireOp",EDGE,"E6");var subQ3=sQuery(id+"F0.wireOp",EDGE,"E5");var subQ4=sQuery(id+"F0.wireOp",EDGE,"E4");var subQ5=sQuery(id+"F0.wireOp",EDGE,"E1.bottom");var subQ6=sQuery(id+"F0.wireOp",EDGE,"E21.filletArc");var subQ7=sQuery(id+"F0.wireOp",EDGE,"E1.top");var subQ8=sQuery(id+"F0.wireOp",EDGE,"E1.left");var subQ9=sQuery(id+"F0.wireOp",EDGE,"E1.right");var subQ10=sQuery(id+"F0.wireOp",EDGE,"E23.filletArc");var subQ11=sQuery(id+"F0.wireOp",EDGE,"E24.filletArc");Q0=makeQuery(id+"F2.boolean.opBoolean","SPLIT",FACE,{"disambiguationData":[TD([makeQuery(id+"F1.opExtrude","SWEPT_FACE",FACE,{"disambiguationData":[OSD([subQ5])]})])],"derivedFrom":makeQuery(id+"F1.opExtrude","CAP_FACE",FACE,{"disambiguationData":[OSD([subQ5,subQ7,subQ8,subQ9,subQ4,subQ3,subQ2,subQ1,subQ6,subQ0,subQ10,subQ11])],"isStart":true})});}
            var sketch = newSketch(context, id + "F16", { "sketchPlane" : qUnion([Q0])});
            skArc(sketch, "E79.0", {"start": v(-70, 90) * mm, "mid": v(-77.07, 87.07) * mm, "end": v(-80, 80) * mm});
            skLineSegment(sketch, "E79.1", {"start": v(-70, 90) * mm, "end": v(70, 90) * mm});
            skLineSegment(sketch, "E79.2", {"start": v(-80, -80) * mm, "end": v(-80, 80) * mm});
            skArc(sketch, "E79.3", {"start": v(-80, -80) * mm, "mid": v(-77.07, -87.07) * mm, "end": v(-70, -90) * mm});
            skArc(sketch, "E79.4", {"start": v(70, -90) * mm, "mid": v(77.07, -87.07) * mm, "end": v(80, -80) * mm});
            skLineSegment(sketch, "E79.5", {"start": v(80, -80) * mm, "end": v(80, 80) * mm});
            skArc(sketch, "E79.6", {"start": v(80, 80) * mm, "mid": v(77.07, 87.07) * mm, "end": v(70, 90) * mm});
            skPoint(sketch, "E79.7", {"position": v(-80, -80) * mm});
            skPoint(sketch, "E79.8", {"position": v(-70, -90) * mm});
            skLineSegment(sketch, "E79.9", {"start": v(-70, -90) * mm, "end": v(70, -90) * mm});
            skPoint(sketch, "E79.10", {"position": v(70, -90) * mm});
            skPoint(sketch, "E79.11", {"position": v(80, -80) * mm});
            skPoint(sketch, "E79.12", {"position": v(80, 80) * mm});
            skPoint(sketch, "E79.13", {"position": v(70, 90) * mm});
            skPoint(sketch, "E79.14", {"position": v(-70, 90) * mm});
            skPoint(sketch, "E79.15", {"position": v(-80, 80) * mm});
            skLineSegment(sketch, "E79.16", {"start": v(-60, 40.3) * mm, "end": v(-60, -40.3) * mm});
            skArc(sketch, "E79.17", {"start": v(-60, -40.3) * mm, "mid": v(-58.99, -44.68) * mm, "end": v(-56.15, -48.18) * mm});
            skArc(sketch, "E79.18", {"start": v(-56.15, -48.18) * mm, "mid": v(0, -67.5) * mm, "end": v(56.15, -48.18) * mm});
            skArc(sketch, "E79.19", {"start": v(56.15, -48.18) * mm, "mid": v(58.99, -44.68) * mm, "end": v(60, -40.3) * mm});
            skLineSegment(sketch, "E79.20", {"start": v(60, 40.3) * mm, "end": v(60, -40.3) * mm});
            skArc(sketch, "E79.21", {"start": v(56.15, 48.18) * mm, "mid": v(0, 67.5) * mm, "end": v(-56.15, 48.18) * mm});
            skArc(sketch, "E79.22", {"start": v(60, 40.3) * mm, "mid": v(58.99, 44.68) * mm, "end": v(56.15, 48.18) * mm});
            skPoint(sketch, "E79.23", {"position": v(60, 40.3) * mm});
            skPoint(sketch, "E79.24", {"position": v(56.15, 48.18) * mm});
            skArc(sketch, "E79.25", {"start": v(-56.15, 48.18) * mm, "mid": v(-58.99, 44.68) * mm, "end": v(-60, 40.3) * mm});
            skPoint(sketch, "E79.26", {"position": v(-56.15, 48.18) * mm});
            skPoint(sketch, "E79.27", {"position": v(-60, 40.3) * mm});
            skPoint(sketch, "E79.28", {"position": v(-60, -40.3) * mm});
            skPoint(sketch, "E79.29", {"position": v(-56.15, -48.18) * mm});
            skPoint(sketch, "E79.30", {"position": v(56.15, -48.18) * mm});
            skPoint(sketch, "E79.31", {"position": v(60, -40.3) * mm});
            skCircle(sketch, "E79.32", {"center": v(60, 67.5) * mm, "radius": 4 * mm});
            skCircle(sketch, "E79.33", {"center": v(-60, 67.5) * mm, "radius": 4 * mm});
            skCircle(sketch, "E79.34", {"center": v(-60, -67.5) * mm, "radius": 4 * mm});
            skCircle(sketch, "E79.35", {"center": v(60, -67.5) * mm, "radius": 4 * mm});
            skPoint(sketch, "E79.36", {"position": v(-77.07, -87.07) * mm});
            skPoint(sketch, "E79.37", {"position": v(77.07, -87.07) * mm});
            skPoint(sketch, "E79.38", {"position": v(77.07, 87.07) * mm});
            skPoint(sketch, "E79.39", {"position": v(-77.07, 87.07) * mm});
            skPoint(sketch, "E79.40", {"position": v(58.99, -44.68) * mm});
            skPoint(sketch, "E79.41", {"position": v(58.99, 44.68) * mm});
            skPoint(sketch, "E79.42", {"position": v(-58.99, 44.68) * mm});
            skPoint(sketch, "E79.43", {"position": v(-58.99, -44.68) * mm});
            skLineSegment(sketch, "E80", {"start": v(0, 23.75) * mm, "end": v(0, 120.23) * mm, "construction": true});
            skPoint(sketch, "E80.endSnap0", {"position": v(0, 90) * mm});
            skCircle(sketch, "E81", {"center": v(0, 120.23) * mm, "radius": 6 * mm});
            skLineSegment(sketch, "E82", {"start": v(-15, 120) * mm, "end": v(-15, 108) * mm});
            skLineSegment(sketch, "E83", {"start": v(-15, 108) * mm, "end": v(-33, 90) * mm});
            skLineSegment(sketch, "E84.MirrorCS", {"start": v(15, 108) * mm, "end": v(33, 90) * mm});
            skLineSegment(sketch, "E85.MirrorCS", {"start": v(15, 120) * mm, "end": v(15, 108) * mm});
            skArc(sketch, "E86", {"start": v(15, 120) * mm, "mid": v(0, 135) * mm, "end": v(-15, 120) * mm});
            skLineSegment(sketch, "E87", {"start": v(-80, 0) * mm, "end": v(80, 0) * mm, "construction": true});
            skArc(sketch, "E88.MirrorCS", {"start": v(15, -120) * mm, "mid": v(0, -135) * mm, "end": v(-15, -120) * mm});
            skLineSegment(sketch, "E89.MirrorCS", {"start": v(15, -108) * mm, "end": v(33, -90) * mm});
            skLineSegment(sketch, "E90.MirrorCS", {"start": v(-15, -108) * mm, "end": v(-33, -90) * mm});
            skArc(sketch, "E91.MirrorCS", {"start": v(-15, 120) * mm, "mid": v(0, 135) * mm, "end": v(15, 120) * mm});
            skLineSegment(sketch, "E92.MirrorCS", {"start": v(80, 0) * mm, "end": v(-80, 0) * mm, "construction": true});
            skLineSegment(sketch, "E93", {"start": v(-15, -108) * mm, "end": v(-15, -120) * mm});
            skLineSegment(sketch, "E94", {"start": v(15, -120) * mm, "end": v(15, -108) * mm});
            skCircle(sketch, "E95.MirrorC", {"center": v(0, -120.23) * mm, "radius": 6 * mm});
            skLineSegment(sketch, "E96.MirrorCS", {"start": v(0, -23.75) * mm, "end": v(0, -120.23) * mm, "construction": true});
            skPoint(sketch, "E97.MirrorP", {"position": v(0, -90) * mm});
            skSolve(sketch);
        }
        {
            var Q0;
            Q0 = qSketchRegion(id + "F16", true);
            var Q1;
            Q1=makeQuery(id+"F2.opExtrude","CAP_FACE",FACE,{"disambiguationData":[OSD([sQuery(id+"F0.wireOp",EDGE,"E12"),sQuery(id+"F0.wireOp",EDGE,"E13"),sQuery(id+"F0.wireOp",EDGE,"E14"),sQuery(id+"F0.wireOp",EDGE,"E15"),sQuery(id+"F0.wireOp",EDGE,"E17.filletArc"),sQuery(id+"F0.wireOp",EDGE,"E18.filletArc"),sQuery(id+"F0.wireOp",EDGE,"E19.filletArc"),sQuery(id+"F0.wireOp",EDGE,"E20.filletArc"),sQuery(id+"F0.wireOp",EDGE,"E25.0"),sQuery(id+"F0.wireOp",EDGE,"E25.1"),sQuery(id+"F0.wireOp",EDGE,"E25.2"),sQuery(id+"F0.wireOp",EDGE,"E25.3"),sQuery(id+"F0.wireOp",EDGE,"E25.4"),sQuery(id+"F0.wireOp",EDGE,"E25.5"),sQuery(id+"F0.wireOp",EDGE,"E25.6"),sQuery(id+"F0.wireOp",EDGE,"E25.7")])],"isStart":false});
            extrude(context, id + "F17", {"entities" : qUnion([Q0]), "operationType" : NewBodyOperationType.ADD, "endBound" : BoundingType.UP_TO_SURFACE, "endBoundEntityFace" : qUnion([Q1]), "depth" : 25 * mm});
        }
    });
